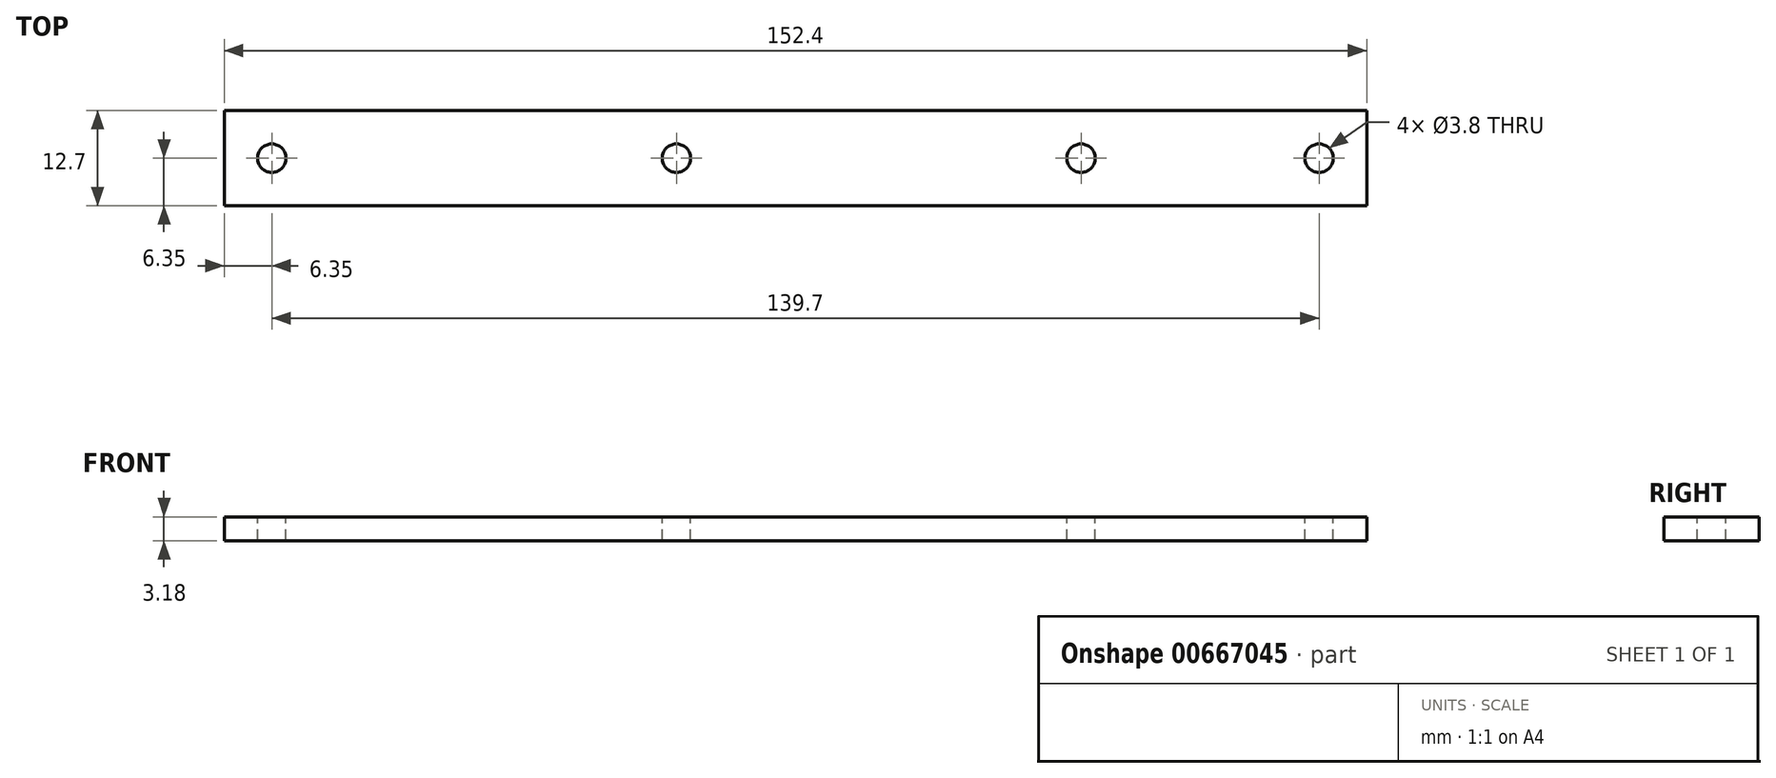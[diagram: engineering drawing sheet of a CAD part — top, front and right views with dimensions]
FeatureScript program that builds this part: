
annotation { "Feature Type Name" : "Feature", "Feature Type Description" : "" }
export const myFeature = defineFeature(function(context is Context, id is Id, definition is map)
    precondition{}
    {
        {
            var Q0;
            Q0=qCreatedBy(makeId("Top.planeOp"),FACE);
            var sketch = newSketch(context, id + "F0", { "sketchPlane" : qUnion([Q0])});
            skLineSegment(sketch, "E0.bottom", {"start": v(-76.2, 6.35) * mm, "end": v(76.2, 6.35) * mm});
            skLineSegment(sketch, "E0.top", {"start": v(-76.2, -6.35) * mm, "end": v(76.2, -6.35) * mm});
            skLineSegment(sketch, "E0.left", {"start": v(-76.2, 6.35) * mm, "end": v(-76.2, -6.35) * mm});
            skLineSegment(sketch, "E0.right", {"start": v(76.2, 6.35) * mm, "end": v(76.2, -6.35) * mm});
            skPoint(sketch, "E0.middle", {"position": v(0, 0) * mm});
            skLineSegment(sketch, "E1", {"start": v(-76.2, 0) * mm, "end": v(76.2, 0) * mm, "construction": true});
            skPoint(sketch, "E2", {"position": v(-69.85, 0) * mm});
            skPoint(sketch, "E3", {"position": v(-15.88, 0) * mm});
            skPoint(sketch, "E4", {"position": v(38.1, 0) * mm});
            skPoint(sketch, "E5", {"position": v(69.85, 0) * mm});
            skSolve(sketch);
        }
        {
            var Q0;
            Q0=makeQuery(id+"F0.imprint","IMPRINT",FACE,{"disambiguationData":[TD([[makeQuery(id+"F0.imprint","IMPRINT",EDGE,{"derivedFrom":sQuery(id+"F0.wireOp",EDGE,"E0.bottom")}),-1.0]])]});
            extrude(context, id + "F1", {"entities" : qUnion([Q0]), "endBound" : BoundingType.SYMMETRIC, "depth" : 3.17 * mm, "offsetDistance" : 25.4 * mm});
        }
        {
            var Q0;
            Q0=makeQuery(id+"F1.opExtrude","CAP_FACE",FACE,{"disambiguationData":[OSD([sQuery(id+"F0.wireOp",EDGE,"E0.bottom"),sQuery(id+"F0.wireOp",EDGE,"E0.top"),sQuery(id+"F0.wireOp",EDGE,"E0.left"),sQuery(id+"F0.wireOp",EDGE,"E0.right")])],"isStart":false});
            var sketch = newSketch(context, id + "F2", { "sketchPlane" : qUnion([Q0])});
            skPoint(sketch, "E6.0", {"position": v(-69.85, 0) * mm});
            skPoint(sketch, "E7.0", {"position": v(-15.88, 0) * mm});
            skPoint(sketch, "E8.0", {"position": v(38.1, 0) * mm});
            skPoint(sketch, "E9.0", {"position": v(69.85, 0) * mm});
            skLineSegment(sketch, "E10.0", {"start": v(-76.2, 0) * mm, "end": v(76.2, 0) * mm});
            skSolve(sketch);
        }
        {
            var Q0;
            Q0=sQuery(id+"F2.wireOp",VERTEX,"E6.0");
            var Q1;
            Q1=sQuery(id+"F2.wireOp",VERTEX,"E7.0");
            var Q2;
            Q2=sQuery(id+"F2.wireOp",VERTEX,"E8.0");
            var Q3;
            Q3=sQuery(id+"F2.wireOp",VERTEX,"E9.0");
            var Q4;
            Q4=makeQuery(id+"F1.opExtrude","SWEPT_BODY",BODY,{"disambiguationData":[OSD([sQuery(id+"F0.wireOp",EDGE,"E0.bottom"),sQuery(id+"F0.wireOp",EDGE,"E0.top"),sQuery(id+"F0.wireOp",EDGE,"E0.left"),sQuery(id+"F0.wireOp",EDGE,"E0.right")])]});
            hole(context, id + "F3", {"style" : HoleStyle.SIMPLE, "endStyle" : HoleEndStyle.THROUGH, "standardTappedOrClearance" : lookupTablePath({ "standard" : "ANSI", "fit" : "Normal (ASME)", "size" : "#6", "type" : "Clearance" }), "standardBlindInLast" : lookupTablePath({ "fit" : "Free", "standard" : "ANSI", "size" : "#6", "type" : "Clearance" }), "holeDiameter" : 3.8 * mm, "majorDiameter" : 6.35 * mm, "isTappedThrough" : true, "tappedDepth" : 10.3 * mm, "tapClearance" : 3, "locations" : qUnion([Q0, Q1, Q2, Q3]), "scope" : qUnion([Q4])});
        }
    });
